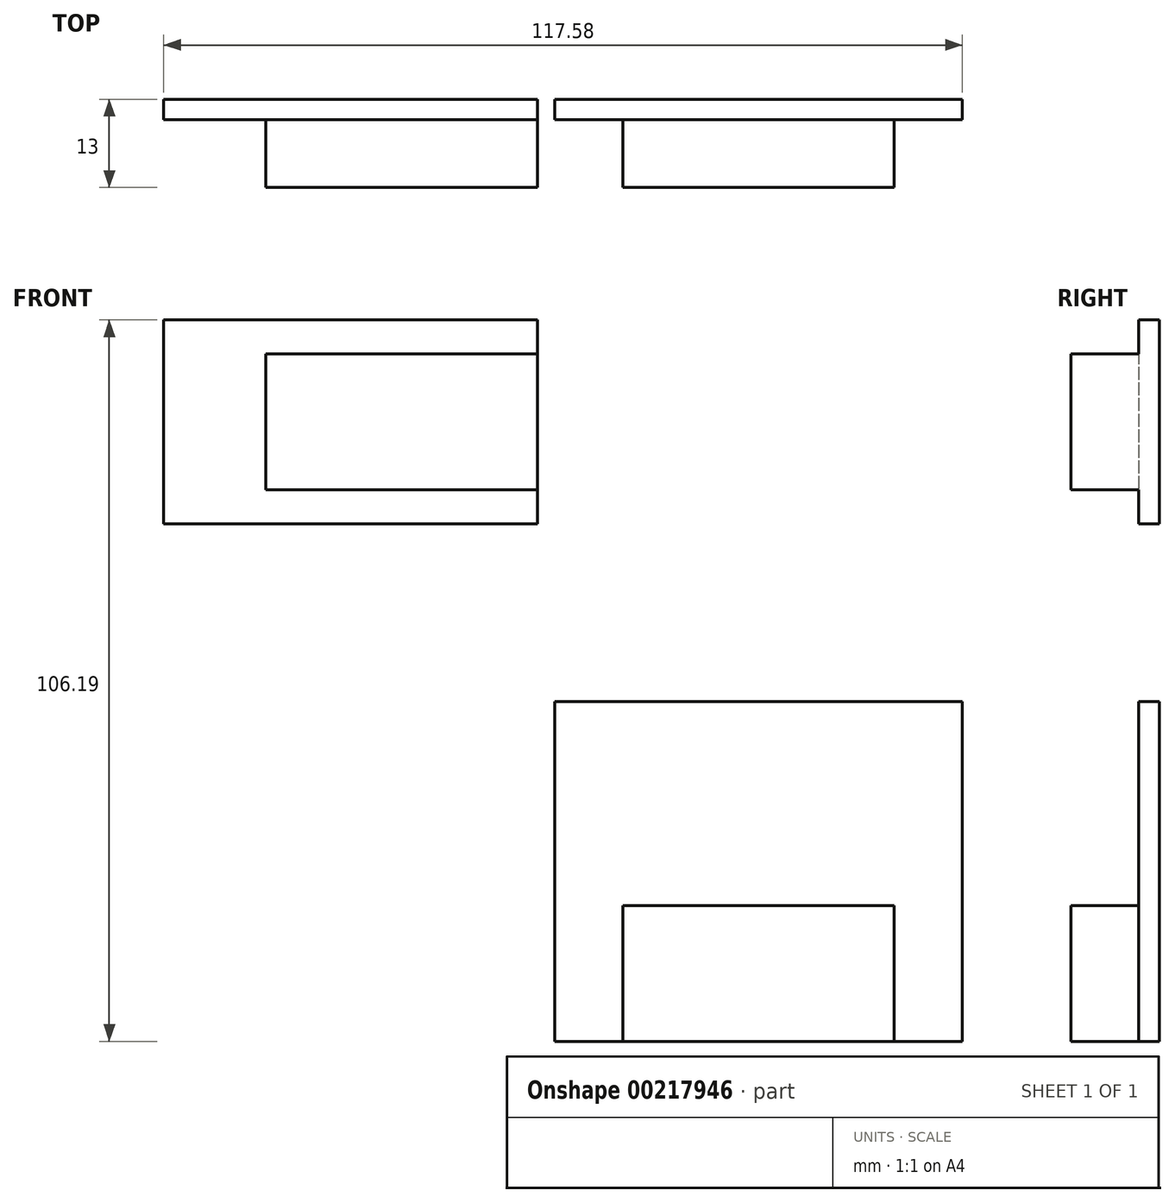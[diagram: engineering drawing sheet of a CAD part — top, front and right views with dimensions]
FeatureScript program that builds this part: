
annotation { "Feature Type Name" : "Feature", "Feature Type Description" : "" }
export const myFeature = defineFeature(function(context is Context, id is Id, definition is map)
    precondition{}
    {
        {
            var Q0;
            Q0=qCreatedBy(makeId("Front.planeOp"),FACE);
            var sketch = newSketch(context, id + "F0", { "sketchPlane" : qUnion([Q0])});
            skLineSegment(sketch, "E0.bottom", {"start": v(-30, 50) * mm, "end": v(30, 50) * mm});
            skLineSegment(sketch, "E0.top", {"start": v(-30, 0) * mm, "end": v(30, 0) * mm});
            skLineSegment(sketch, "E0.left", {"start": v(-30, 50) * mm, "end": v(-30, 0) * mm});
            skLineSegment(sketch, "E0.right", {"start": v(30, 50) * mm, "end": v(30, 0) * mm});
            skLineSegment(sketch, "E1.bottom", {"start": v(-20, 20) * mm, "end": v(20, 20) * mm});
            skLineSegment(sketch, "E1.top", {"start": v(-20, 0) * mm, "end": v(20, 0) * mm});
            skLineSegment(sketch, "E1.left", {"start": v(-20, 20) * mm, "end": v(-20, 0) * mm});
            skLineSegment(sketch, "E1.right", {"start": v(20, 20) * mm, "end": v(20, 0) * mm});
            skLineSegment(sketch, "E2", {"start": v(0, 50) * mm, "end": v(0, 0) * mm, "construction": true});
            skSolve(sketch);
        }
        {
            var Q0;
            Q0=qCreatedBy(makeId("Front.planeOp"),FACE);
            var sketch = newSketch(context, id + "F1", { "sketchPlane" : qUnion([Q0])});
            skLineSegment(sketch, "E3.bottom", {"start": v(-87.58, 106.2) * mm, "end": v(-32.58, 106.2) * mm});
            skLineSegment(sketch, "E3.top", {"start": v(-87.58, 76.2) * mm, "end": v(-32.58, 76.2) * mm});
            skLineSegment(sketch, "E3.left", {"start": v(-87.58, 106.2) * mm, "end": v(-87.58, 76.2) * mm});
            skLineSegment(sketch, "E3.right", {"start": v(-32.58, 106.2) * mm, "end": v(-32.58, 76.2) * mm});
            skLineSegment(sketch, "E4.bottom", {"start": v(-72.58, 101.2) * mm, "end": v(-32.58, 101.2) * mm});
            skLineSegment(sketch, "E4.top", {"start": v(-72.58, 81.2) * mm, "end": v(-32.58, 81.2) * mm});
            skLineSegment(sketch, "E4.left", {"start": v(-72.58, 101.2) * mm, "end": v(-72.58, 81.2) * mm});
            skLineSegment(sketch, "E4.right", {"start": v(-32.58, 101.2) * mm, "end": v(-32.58, 81.2) * mm});
            skLineSegment(sketch, "E5", {"start": v(-32.58, 91.2) * mm, "end": v(-87.58, 91.2) * mm, "construction": true});
            skPoint(sketch, "E5.endSnap0", {"position": v(-72.58, 91.2) * mm});
            skSolve(sketch);
        }
        {
            var Q0;
            Q0=makeQuery(id+"F0.imprint","IMPRINT",FACE,{"disambiguationData":[TD([[makeQuery(id+"F0.imprint","IMPRINT",EDGE,{"derivedFrom":sQuery(id+"F0.wireOp",EDGE,"E0.bottom")}),-1.0]])]});
            var Q1;
            Q1=makeQuery(id+"F0.imprint","IMPRINT",FACE,{"disambiguationData":[TD([[makeQuery(id+"F0.imprint","IMPRINT",EDGE,{"derivedFrom":sQuery(id+"F0.wireOp",EDGE,"E1.bottom")}),-1.0]])]});
            var Q2;
            {var subQ1=sQuery(id+"F1.wireOp",EDGE,"E3.bottom");Q2=makeQuery(id+"F1.imprint","IMPRINT",FACE,{"disambiguationData":[TD([[makeQuery(id+"F1.imprint","IMPRINT",EDGE,{"derivedFrom":subQ1}),-1.0]])]});}
            var Q3;
            Q3=makeQuery(id+"F1.imprint","IMPRINT",FACE,{"disambiguationData":[TD([[makeQuery(id+"F1.imprint","IMPRINT",EDGE,{"derivedFrom":sQuery(id+"F1.wireOp",EDGE,"E4.bottom")}),-1.0]])]});
            extrude(context, id + "F2", {"entities" : qUnion([Q0, Q1, Q2, Q3]), "oppositeDirection" : true, "depth" : 3 * mm});
        }
        {
            var Q0;
            Q0=makeQuery(id+"F0.imprint","IMPRINT",FACE,{"disambiguationData":[TD([[makeQuery(id+"F0.imprint","IMPRINT",EDGE,{"derivedFrom":sQuery(id+"F0.wireOp",EDGE,"E1.bottom")}),-1.0]])]});
            var Q1;
            Q1=makeQuery(id+"F1.imprint","IMPRINT",FACE,{"disambiguationData":[TD([[makeQuery(id+"F1.imprint","IMPRINT",EDGE,{"derivedFrom":sQuery(id+"F1.wireOp",EDGE,"E4.bottom")}),-1.0]])]});
            extrude(context, id + "F3", {"entities" : qUnion([Q0, Q1]), "operationType" : NewBodyOperationType.ADD, "depth" : 10 * mm});
        }
    });
